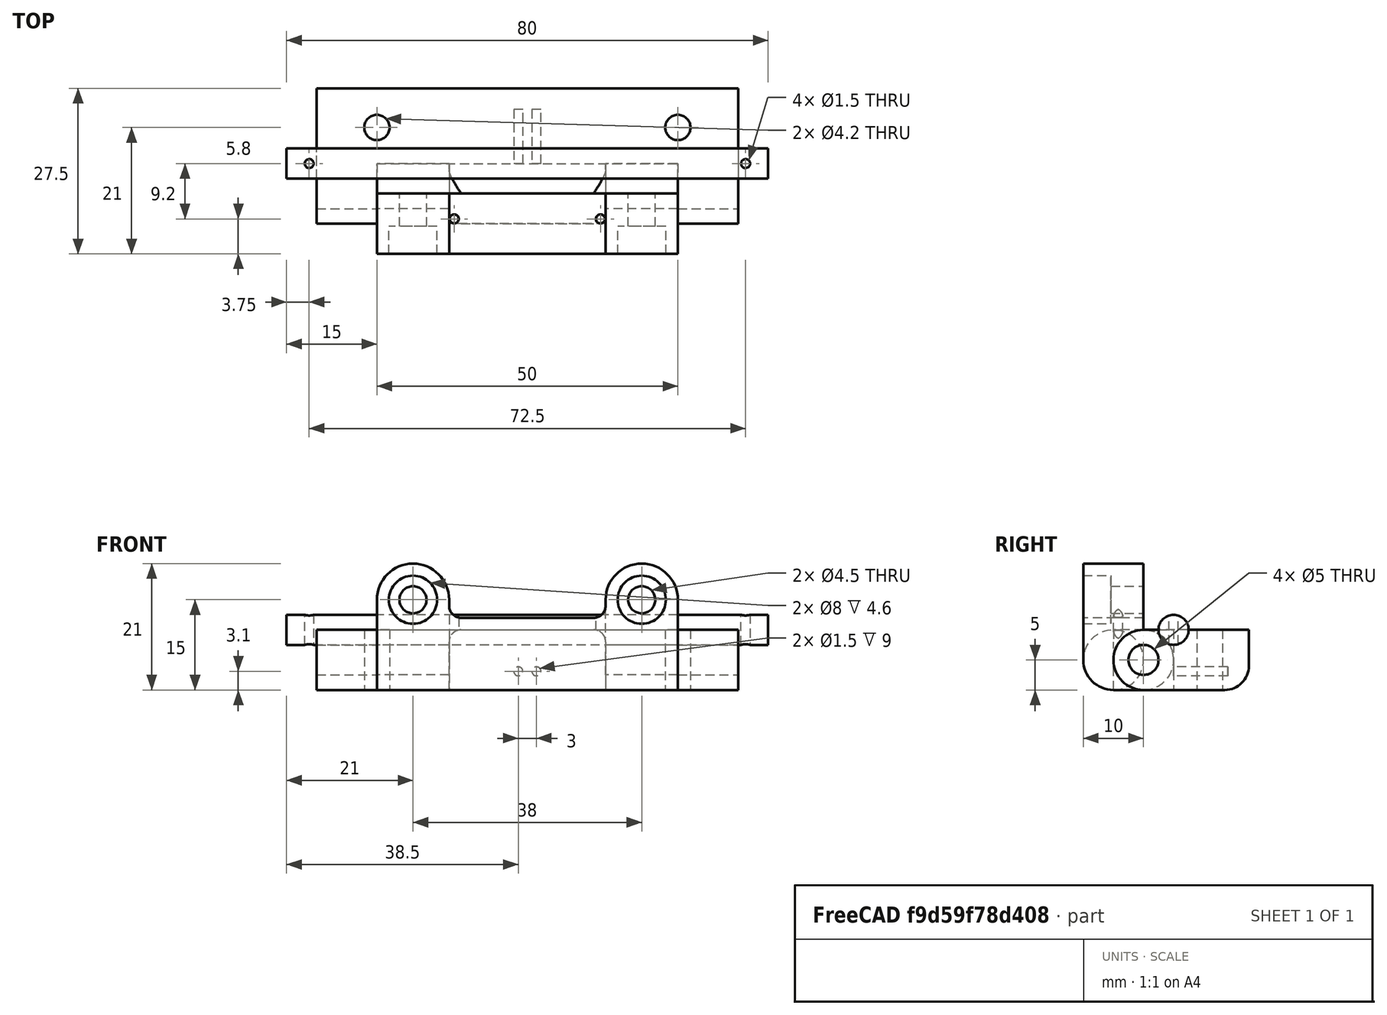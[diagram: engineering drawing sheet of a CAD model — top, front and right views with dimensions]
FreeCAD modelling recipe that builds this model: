
FCSTD DOCUMENT  (FreeCAD 0.18R14555 (Git shallow))
Label: hinge
License: All rights reserved
LicenseURL: http://en.wikipedia.org/wiki/All_rights_reserved
objects: TechDraw::DrawViewDimension×17, Sketcher::SketchObject×11, PartDesign::Pocket×6, TechDraw::DrawProjGroupItem×6, PartDesign::Pad×3, TechDraw::DrawProjGroup×3, PartDesign::Body×3, PartDesign::Hole×2, TechDraw::DrawSVGTemplate×2, TechDraw::DrawViewAnnotation×2, TechDraw::DrawViewSymbol×2, TechDraw::DrawViewPart×2, TechDraw::DrawPage×2, PartDesign::Plane×1, PartDesign::Fillet×1, TechDraw::DrawViewSection×1
note: 38 computed .brp shape members not serialized (recipe doc carries the construction recipe); baked Part::Feature solids carry a one-line shape summary decoded from their .brp

FEATURE [Sketcher::SketchObject] Sketch001
  MapMode = 5
  Support = -> [XY_Plane001]
  sketch-geometry (8):
    g0: LineSegment StartX=-35 StartY=-10 StartZ=0 EndX=-35 EndY=12.5 EndZ=0
    g1: LineSegment StartX=-35 StartY=12.5 StartZ=0 EndX=35 EndY=12.5 EndZ=0
    g2: LineSegment StartX=35 StartY=12.5 StartZ=0 EndX=35 EndY=-10 EndZ=0
    g3: LineSegment StartX=35 StartY=-10 StartZ=0 EndX=25 EndY=-10 EndZ=0
    g4: LineSegment StartX=25 StartY=-10 StartZ=0 EndX=25 EndY=0 EndZ=0
    g5: LineSegment StartX=-35 StartY=-10 StartZ=0 EndX=-25 EndY=-10 EndZ=0
    g6: LineSegment StartX=-25 StartY=-10 StartZ=0 EndX=-25 EndY=0 EndZ=0
    g7: LineSegment StartX=-25 StartY=0 StartZ=0 EndX=25 EndY=0 EndZ=0
  constraints (22):
    c: Vertical(g0)
    c: Coincident(g0,g1)
    c: Coincident(g1,g2)
    c: Vertical(g2)
    c: Coincident(g2,g3)
    c: Horizontal(g3)
    c: Coincident(g3,g4)
    c: PointOnObject(g4,g-1)
    c: Coincident(g0,g5)
    c: Horizontal(g5)
    c: Coincident(g5,g6)
    c: PointOnObject(g6,g-1)
    c: Vertical(g6)
    c: Vertical(g4)
    c: Symmetric(g1,g0,g-2)
    c: Symmetric(g3,g5,g-2)
    c: Coincident(g7,g4)
    c: DistanceX(g5,g5) = 10
    c: DistanceY(g6,g6) = 10
    c: Coincident(g7,g6)
    c: DistanceX(g5,g3) = 50
    c: DistanceY(g-1,g1) = 12.5
FEATURE [PartDesign::Pad] Pad001
  Length = 10
  Length2 = 100
  Profile = -> Sketch001
  Reversed = true
  Type = 0
FEATURE [Sketcher::SketchObject] Sketch002
  MapMode = 5
  Placement = pos=(0,0,0) rot=(0.57735,0.57735,0.57735;2.0944rad)
  Support = -> [YZ_Plane001]
  sketch-geometry (10):
    g0: Circle CenterX=-5 CenterY=-5 CenterZ=0 NormalX=0 NormalY=0 NormalZ=1 AngleXU=0 Radius=2.5
    g1: ArcOfCircle CenterX=-5 CenterY=-5 CenterZ=0 NormalX=0 NormalY=0 NormalZ=1 AngleXU=0 Radius=5 StartAngle=1.5708 EndAngle=3.14159
    g2: LineSegment [constr] StartX=-10 StartY=-5 StartZ=0 EndX=-10 EndY=0 EndZ=0
    g3: LineSegment StartX=-10 StartY=0 StartZ=0 EndX=-5 EndY=0 EndZ=0
    g4: LineSegment StartX=-10 StartY=-10 StartZ=0 EndX=-5 EndY=-10 EndZ=0
    g5: ArcOfCircle CenterX=-5 CenterY=-5 CenterZ=0 NormalX=0 NormalY=0 NormalZ=1 AngleXU=0 Radius=5 StartAngle=3.14159 EndAngle=4.71239
    g6: LineSegment [constr] StartX=-10 StartY=-5 StartZ=0 EndX=-10 EndY=-10 EndZ=0
    g7: LineSegment StartX=-10 StartY=0 StartZ=0 EndX=-13 EndY=0 EndZ=0
    g8: LineSegment StartX=-13 StartY=0 StartZ=0 EndX=-13 EndY=-10 EndZ=0
    g9: LineSegment StartX=-13 StartY=-10 StartZ=0 EndX=-10 EndY=-10 EndZ=0
  constraints (27):
    c: Diameter(g0) = 5
    c: Coincident(g1,g0)
    c: Vertical(g2)
    c: Coincident(g3,g2)
    c: Tangent(g3,g1) = 1.5708
    c: Coincident(g1,g3)
    c: Horizontal(g3)
    c: DistanceX(g0,g-1) = 5
    c: PointOnObject(g2,g-1)
    c: DistanceY(g0,g-1) = 5
    c: Horizontal(g4)
    c: Tangent(g1,g5) = -1.5708
    c: Tangent(g1,g2) = 1.5708
    c: Coincident(g6,g1)
    c: Vertical(g6)
    c: Coincident(g4,g6)
    c: Equal(g6,g2)
    c: Coincident(g3,g7)
    c: Coincident(g7,g8)
    c: Vertical(g8)
    c: Coincident(g8,g9)
    c: Coincident(g9,g4)
    c: Horizontal(g9)
    c: Horizontal(g7)
    c: DistanceX(g1,g0) = 5
    c: DistanceX(g9,g9) = 3
    c: Tangent(g5,g4) = -1.5708
FEATURE [PartDesign::Pocket] Pocket
  BaseFeature = -> Pad001
  Length = 5
  Length2 = 100
  Midplane = true
  Profile = -> Sketch002
  Type = 1
FEATURE [Sketcher::SketchObject] Sketch007
  MapMode = 5
  Support = -> [XY_Plane001]
  sketch-geometry (5):
    g0: Circle [constr] CenterX=0 CenterY=6 CenterZ=0 NormalX=0 NormalY=0 NormalZ=1 AngleXU=0 Radius=2.1
    g1: Circle CenterX=25 CenterY=6 CenterZ=0 NormalX=0 NormalY=0 NormalZ=1 AngleXU=0 Radius=2.1
    g2: Circle CenterX=-25 CenterY=6 CenterZ=0 NormalX=0 NormalY=0 NormalZ=1 AngleXU=0 Radius=2.1
    g3: LineSegment [constr] StartX=0 StartY=6 StartZ=0 EndX=25 EndY=6 EndZ=0
    g4: LineSegment [constr] StartX=0 StartY=6 StartZ=0 EndX=-25 EndY=6 EndZ=0
  constraints (13):
    c: PointOnObject(g0,g-2)
    c: Coincident(g3,g0)
    c: Coincident(g3,g1)
    c: Coincident(g4,g0)
    c: Coincident(g4,g2)
    c: Horizontal(g3)
    c: Horizontal(g4)
    c: Equal(g4,g3)
    c: DistanceX(g2,g1) = 50
    c: Diameter(g0) = 4.2
    c: Equal(g0,g1)
    c: Equal(g0,g2)
    c: DistanceY(g-1,g0) = 6
FEATURE [PartDesign::Hole] Hole
  BaseFeature = -> Pocket
  Depth = 25
  DepthType = 1
  Diameter = 4.2
  DrillPoint = 1
  DrillPointAngle = 118
  HoleCutCountersinkAngle = 90
  HoleCutDepth = 0
  HoleCutDiameter = 0
  HoleCutType = 0
  ModelActualThread = false
  Profile = -> Sketch007
  Tapered = false
  TaperedAngle = 90
  ThreadAngle = 0
  ThreadClass = 0
  ThreadCutOffInner = 0
  ThreadCutOffOuter = 0
  ThreadDirection = 0
  ThreadFit = 0
  ThreadPitch = 0
  ThreadSize = 0
  ThreadType = 0
  Threaded = false
FEATURE [Sketcher::SketchObject] Sketch
  MapMode = 5
  Placement = pos=(0,0,0) rot=(0.57735,0.57735,0.57735;2.0944rad)
  Support = -> [YZ_Plane]
  sketch-geometry (7):
    g0: Circle CenterX=-5 CenterY=-5 CenterZ=0 NormalX=0 NormalY=0 NormalZ=1 AngleXU=0 Radius=2.5
    g1: ArcOfCircle CenterX=-5 CenterY=-5 CenterZ=0 NormalX=0 NormalY=0 NormalZ=1 AngleXU=0 Radius=5 StartAngle=4.71239 EndAngle=7.85398
    g2: LineSegment StartX=-4.99997 StartY=12 StartZ=0 EndX=-15 EndY=12 EndZ=0
    g3: LineSegment StartX=-15 StartY=12 StartZ=0 EndX=-15 EndY=-5 EndZ=0
    g4: LineSegment StartX=-9.99997 StartY=-10 StartZ=0 EndX=-5 EndY=-10 EndZ=0
    g5: LineSegment StartX=-4.99997 StartY=-8.94778e-11 StartZ=0 EndX=-4.99997 EndY=12 EndZ=0
    g6: ArcOfCircle CenterX=-9.99997 CenterY=-5 CenterZ=0 NormalX=0 NormalY=0 NormalZ=1 AngleXU=0 Radius=5 StartAngle=3.14159 EndAngle=4.71239
  constraints (20):
    c: DistanceX(g0,g-1) = 5
    c: DistanceY(g0,g-1) = 5
    c: Diameter(g0) = 5
    c: Coincident(g1,g0)
    c: PointOnObject(g1,g-1)
    c: Radius(g1) = 5
    c: Horizontal(g2)
    c: Coincident(g2,g3)
    c: Vertical(g3)
    c: Coincident(g4,g1)
    c: Horizontal(g4)
    c: DistanceY(g1,g2) = 12
    c: DistanceY(g1,g0) = 5
    c: DistanceX(g2,g2) = 10
    c: Coincident(g5,g2)
    c: Vertical(g5)
    c: Tangent(g4,g6) = -1.5708
    c: Tangent(g3,g6) = -1.5708
    c: Radius(g6) = 5
    c: Coincident(g5,g1)
FEATURE [PartDesign::Pad] Pad
  Length = 50
  Length2 = 100
  Midplane = true
  Placement = pos=(0,0,0) rot=(0.57735,0.57735,0.57735;2.0944rad)
  Profile = -> Sketch
  Type = 0
FEATURE [Sketcher::SketchObject] Sketch010
  MapMode = 5
  Placement = pos=(0,0,0) rot=(1,0,0;1.5708rad)
  Support = -> [XZ_Plane]
  sketch-geometry (14):
    g0: LineSegment StartX=13 StartY=5 StartZ=0 EndX=13 EndY=4 EndZ=0
    g1: LineSegment StartX=-13 StartY=4 StartZ=0 EndX=-13 EndY=5 EndZ=0
    g2: ArcOfCircle CenterX=-19 CenterY=5 CenterZ=0 NormalX=0 NormalY=0 NormalZ=1 AngleXU=0 Radius=6 StartAngle=1e-16 EndAngle=3.14159
    g3: ArcOfCircle CenterX=19 CenterY=5 CenterZ=0 NormalX=0 NormalY=0 NormalZ=1 AngleXU=0 Radius=6 StartAngle=0 EndAngle=3.14159
    g4: LineSegment [constr] StartX=25 StartY=5 StartZ=0 EndX=-25 EndY=5 EndZ=0
    g5: LineSegment StartX=25 StartY=5 StartZ=0 EndX=25 EndY=11 EndZ=0
    g6: LineSegment [constr] StartX=25 StartY=11 StartZ=0 EndX=-25 EndY=11 EndZ=0
    g7: LineSegment StartX=-25 StartY=11 StartZ=0 EndX=-25 EndY=5 EndZ=0
    g8: LineSegment StartX=-25 StartY=11 StartZ=0 EndX=-25 EndY=12 EndZ=0
    g9: LineSegment StartX=-25 StartY=12 StartZ=0 EndX=25 EndY=12 EndZ=0
    g10: LineSegment StartX=25 StartY=12 StartZ=0 EndX=25 EndY=11 EndZ=0
    g11: LineSegment StartX=-11 StartY=2 StartZ=0 EndX=11 EndY=2 EndZ=0
    g12: ArcOfCircle CenterX=-11 CenterY=4 CenterZ=0 NormalX=0 NormalY=0 NormalZ=1 AngleXU=0 Radius=2 StartAngle=3.14159 EndAngle=4.71239
    g13: ArcOfCircle CenterX=11 CenterY=4 CenterZ=0 NormalX=0 NormalY=0 NormalZ=1 AngleXU=0 Radius=2 StartAngle=4.71239 EndAngle=6.28319
  constraints (39):
    c: Vertical(g0)
    c: Vertical(g1)
    c: Symmetric(g0,g1,g-2)
    c: DistanceX(g1,g0) = 26
    c: Coincident(g2,g1)
    c: Coincident(g3,g0)
    c: Coincident(g4,g3)
    c: Coincident(g4,g2)
    c: Horizontal(g4)
    c: PointOnObject(g2,g4)
    c: PointOnObject(g1,g4)
    c: PointOnObject(g3,g4)
    c: Equal(g3,g2)
    c: DistanceX(g4,g4) = 50
    c: Coincident(g3,g5)
    c: Coincident(g5,g6)
    c: Horizontal(g6)
    c: Coincident(g6,g7)
    c: Coincident(g7,g2)
    c: Vertical(g7)
    c: DistanceY(g-1,g6) = 11
    c: Coincident(g7,g8)
    c: Vertical(g8)
    c: Coincident(g8,g9)
    c: Horizontal(g9)
    c: Coincident(g9,g10)
    c: Coincident(g10,g5)
    c: Vertical(g10)
    c: Vertical(g5)
    c: DistanceY(g8,g8) = 1
    c: Tangent(g2,g6)
    c: Horizontal(g11)
    c: Tangent(g1,g12) = 1.5708
    c: Tangent(g11,g12) = -1.5708
    c: Radius(g12) = 2
    c: DistanceY(g-1,g11) = 2
    c: Tangent(g0,g13) = 1.5708
    c: Tangent(g11,g13) = -1.5708
    c: Equal(g13,g12)
FEATURE [PartDesign::Plane] DatumPlane001
  AttachmentOffset = pos=(0,0,15) rot=(0,0,1;0rad)
  Length = 56.4768
  MapMode = 5
  Placement = pos=(0,-15,-3.3e-15) rot=(1,0,0;1.5708rad)
  ResizeMode = 0
  Support = -> [XZ_Plane]
  Width = 27.4512
FEATURE [Sketcher::SketchObject] Sketch011
  MapMode = 5
  Placement = pos=(0,-15,-3.3e-15) rot=(1,0,0;1.5708rad)
  Support = -> [DatumPlane001]
  sketch-geometry (2):
    g0: Circle CenterX=-19 CenterY=5 CenterZ=0 NormalX=0 NormalY=0 NormalZ=1 AngleXU=0 Radius=2
    g1: Circle CenterX=19 CenterY=5 CenterZ=0 NormalX=0 NormalY=0 NormalZ=1 AngleXU=0 Radius=2.31769
  constraints (4):
    c: Symmetric(g1,g0,g-2)
    c: DistanceX(g0,g1) = 38
    c: Diameter(g0) = 4
    c: DistanceY(g-1,g0) = 5
FEATURE [Sketcher::SketchObject] Sketch009
  MapMode = 5
  Placement = pos=(0,0,0) rot=(1,0,0;1.5708rad)
  Support = -> [XZ_Plane]
  sketch-geometry (6):
    g0: LineSegment StartX=-11.0007 StartY=0 StartZ=0 EndX=10.9993 EndY=0 EndZ=0
    g1: LineSegment StartX=12.9993 StartY=-2 StartZ=0 EndX=12.9993 EndY=-18.3189 EndZ=0
    g2: LineSegment StartX=12.9993 StartY=-18.3189 StartZ=0 EndX=-13.0007 EndY=-18.3189 EndZ=0
    g3: LineSegment StartX=-13.0007 StartY=-18.3189 StartZ=0 EndX=-13.0007 EndY=-2 EndZ=0
    g4: ArcOfCircle CenterX=10.9993 CenterY=-2 CenterZ=0 NormalX=0 NormalY=0 NormalZ=1 AngleXU=0 Radius=2 StartAngle=0 EndAngle=1.5708
    g5: ArcOfCircle CenterX=-11.0007 CenterY=-2 CenterZ=0 NormalX=0 NormalY=0 NormalZ=1 AngleXU=0 Radius=2 StartAngle=1.5708 EndAngle=3.14159
  constraints (14):
    c: Coincident(g1,g2)
    c: Coincident(g2,g3)
    c: Horizontal(g2)
    c: Vertical(g1)
    c: Vertical(g3)
    c: Tangent(g1,g4) = 1.5708
    c: Tangent(g0,g4) = 1.5708
    c: Tangent(g0,g5) = 1.5708
    c: Tangent(g3,g5) = 1.5708
    c: DistanceX(g3,g1) = 26
    c: Radius(g4) = 2
    c: Equal(g4,g5)
    c: Horizontal(g0)
    c: PointOnObject(g0,g-1)
FEATURE [PartDesign::Pocket] Pocket002
  BaseFeature = -> Pad
  Length = 10
  Length2 = 100
  Placement = pos=(0,0,0) rot=(0.57735,0.57735,0.57735;2.0944rad)
  Profile = -> Sketch009
  Reversed = true
  Type = 0
FEATURE [PartDesign::Pocket] Pocket003
  BaseFeature = -> Pocket002
  Length = 5
  Length2 = 100
  Placement = pos=(0,0,0) rot=(0.57735,0.57735,0.57735;2.0944rad)
  Profile = -> Sketch010
  Reversed = true
  Type = 1
FEATURE [TechDraw::DrawSVGTemplate] Template
  EditableTexts = Designed_by_Name=Papamatthaiou M.; FC-Date=17/01/2020; FC-SC=1:1; FC-SHEET=1/1; FC-Title=PocketQube Static Hinge; MATERIAL=NOTE-4; REV=B; ROUGHNESS=-; Subtitle=StatikHinge; TOLERANCES=DIN ISO 2768-mk; Weight=~26.56g
  Height = 210
  Orientation = 1
  Width = 297
FEATURE [TechDraw::DrawProjGroup] ProjGroup
  AutoDistribute = true
  LockPosition = false
  ProjectionType = 1
  Rotation = 0
  ScaleType = 2
  X = 168.228
  Y = 97.2357
  spacingX = 15
  spacingY = 15
FEATURE [TechDraw::DrawViewAnnotation] Annotation
  Font = DejaVu Sans
  LineSpace = 80
  LockPosition = false
  MaxWidth = -1
  Rotation = 0
  ScaleType = 0
  Text = Notes: | 1. Drill hole \u23004.2 THRU | 2. Mating hole (H7) for part P/N:  | MISUMI  SCLGN5-70 Shaft Dia. D: 5.00,  | Tolerance: g6 (sliding fit) | 3. This part is mating with parts DoorHinge | and with y-plate | 4. Material: Al 7075 | 5. Drill hole \u23001.5 THRU. Mating holes  | for torsional springs
  TextSize = 6
  TextStyle = 0
  X = 77.2478
  Y = 49.013
FEATURE [PartDesign::Hole] Hole001
  BaseFeature = -> Pocket003
  Depth = 25
  DepthType = 1
  Diameter = 4.5
  DrillPoint = 1
  DrillPointAngle = 118
  HoleCutCountersinkAngle = 90
  HoleCutDepth = 4.6
  HoleCutDiameter = 8
  HoleCutType = 1
  ModelActualThread = false
  Placement = pos=(0,0,0) rot=(0.57735,0.57735,0.57735;2.0944rad)
  Profile = -> Sketch011
  Tapered = false
  TaperedAngle = 90
  ThreadAngle = 0
  ThreadClass = 0
  ThreadCutOffInner = 0
  ThreadCutOffOuter = 0
  ThreadDirection = 0
  ThreadFit = 0
  ThreadPitch = 0
  ThreadSize = 0
  ThreadType = 0
  Threaded = false
FEATURE [TechDraw::DrawSVGTemplate] Template001
  EditableTexts = Designed_by_Name=Papamatthaiou M.; FC-Date=17/01/2020; FC-SC=1:1; FC-SHEET=1/1; FC-Title=PocketQube Door Hinge; MATERIAL=NOTE-5; REV=B; ROUGHNESS=-; Subtitle=DoorHinge; TOLERANCES=DIN ISO 2768-mk; Weight=~17.21g
  Height = 210
  Orientation = 1
  Width = 297
FEATURE [TechDraw::DrawViewSymbol] Symbol
  LockPosition = false
  Rotation = 0
  ScaleType = 2
  Symbol = <blob: 3150 chars omitted>
  X = 16.0884
  Y = 131.565
FEATURE [TechDraw::DrawViewSymbol] Symbol001
  LockPosition = false
  Rotation = 0
  ScaleType = 2
  Symbol = <blob: 3150 chars omitted>
  X = 22.4016
  Y = 147.366
FEATURE [TechDraw::DrawViewAnnotation] Annotation001
  Font = DejaVu Sans
  LineSpace = 80
  LockPosition = false
  MaxWidth = -1
  Rotation = 0
  ScaleType = 0
  Text = Notes: | 1. Drill hole \u23004.5 THRU | 2. Mating hole (H7) for part P/N:  | MISUMI  SCLGN5-70 Shaft Dia. D: 5.00,  | Tolerance: g6 (sliding fit) | 3. This part is mating with parts DoorHinge | and with door | 4. CBORE \u23008.00 DEEP 4.6 (M4 DIN912) | 5. Material: Al 7075 | 6. Drill Holes \u23001.5 THRU. Mating | holes for torsional springs
  TextSize = 6
  TextStyle = 0
  X = 77.0938
  Y = 51.4062
FEATURE [Sketcher::SketchObject] Sketch012
  MapMode = 5
  Placement = pos=(0,0,0) rot=(1,0,0;1.5708rad)
  Support = -> [XZ_Plane001]
  sketch-geometry (3):
    g0: Circle CenterX=-1.5 CenterY=-6.9 CenterZ=0 NormalX=0 NormalY=0 NormalZ=1 AngleXU=0 Radius=0.75
    g1: Circle CenterX=1.5 CenterY=-6.9 CenterZ=0 NormalX=0 NormalY=0 NormalZ=1 AngleXU=0 Radius=0.75
    g2: GeomPoint X=0 Y=-10 Z=0
  constraints (7):
    c: Diameter(g1) = 1.5
    c: Equal(g1,g0)
    c: Symmetric(g1,g0,g-2)
    c: DistanceX(g0,g1) = 3
    c: PointOnObject(g2,g-2)
    c: DistanceY(g2,g-1) = 10
    c: DistanceY(g2,g1) = 3.1
FEATURE [PartDesign::Pocket] Pocket004
  BaseFeature = -> Hole
  Length = 9
  Length2 = 100
  Profile = -> Sketch012
  Type = 0
FEATURE [PartDesign::Fillet] Fillet
  Base = -> Pocket004 [Edge19]
  BaseFeature = -> Pocket004
  Radius = 4
FEATURE [PartDesign::Body] Body001  label="StatikHinge"
  Group = -> [Sketch001,Pad001,Sketch002,Pocket,Sketch007,Hole,Sketch012,Pocket004,Fillet]
  Origin = -> Origin001
  Tip = -> Fillet
FEATURE [TechDraw::DrawViewPart] View
  CoarseView = false
  Direction = (0.831,-0.177,0.527)
  Focus = 100
  HardHidden = false
  IsoCount = 0
  IsoHidden = false
  IsoVisible = false
  LockPosition = false
  Perspective = false
  Rotation = 0
  ScaleType = 0
  SeamHidden = false
  SeamVisible = false
  SmoothHidden = false
  SmoothVisible = false
  Source = -> [Body001]
  X = 260.762
  Y = 173.153
FEATURE [Sketcher::SketchObject] Sketch013
  MapMode = 5
  Support = -> [XY_Plane]
  sketch-geometry (2):
    g0: Circle CenterX=-12.15 CenterY=-9.2 CenterZ=0 NormalX=0 NormalY=0 NormalZ=1 AngleXU=0 Radius=0.75
    g1: Circle CenterX=12.15 CenterY=-9.2 CenterZ=0 NormalX=0 NormalY=0 NormalZ=1 AngleXU=0 Radius=0.75
  constraints (5):
    c: Diameter(g1) = 1.5
    c: Equal(g1,g0)
    c: Symmetric(g0,g1,g-2)
    c: DistanceX(g0,g1) = 24.3
    c: DistanceY(g1,g-1) = 9.2
FEATURE [PartDesign::Pocket] Pocket005
  BaseFeature = -> Hole001
  Length = 5
  Length2 = 100
  Midplane = true
  Placement = pos=(0,0,0) rot=(0.57735,0.57735,0.57735;2.0944rad)
  Profile = -> Sketch013
  Type = 1
FEATURE [PartDesign::Body] Body  label="DoorHinge"
  Group = -> [Sketch,Pad,Sketch009,Pocket002,Sketch010,Pocket003,DatumPlane001,Sketch011,Hole001,Sketch013,Pocket005]
  Origin = -> Origin
  Tip = -> Pocket005
FEATURE [TechDraw::DrawProjGroupItem] ProjItem002  label="Front001"
  CoarseView = false
  Direction = (0,1,0)
  Focus = 100
  HardHidden = false
  IsoCount = 0
  IsoHidden = false
  IsoVisible = false
  LockPosition = true
  Perspective = false
  Rotation = 0
  RotationVector = (-1,0,0)
  ScaleType = 2
  SeamHidden = false
  SeamVisible = false
  SmoothHidden = false
  SmoothVisible = false
  Source = -> [Body]
  Type = 0
  X = 0
  Y = 0
FEATURE [TechDraw::DrawProjGroupItem] ProjItem003  label="Left001"
  CoarseView = false
  Direction = (1,1e-16,0)
  Focus = 100
  HardHidden = false
  IsoCount = 0
  IsoHidden = false
  IsoVisible = false
  LockPosition = false
  Perspective = false
  Rotation = 0
  RotationVector = (-1e-16,1,0)
  ScaleType = 2
  SeamHidden = false
  SeamVisible = false
  SmoothHidden = false
  SmoothVisible = false
  Source = -> [Body]
  Type = 1
  X = 65
  Y = 0
FEATURE [TechDraw::DrawViewDimension] Dimension007
  Arbitrary = false
  FormatSpec = (Note-1) ⌀%.2f
  LockPosition = false
  MeasureType = 1
  OverTolerance = 0
  References2D = -> [ProjItem002]
  Rotation = 0
  ScaleType = 0
  Type = 5
  UnderTolerance = 0
  X = 5.54075
  Y = 26.0395
FEATURE [TechDraw::DrawViewDimension] Dimension008
  Arbitrary = false
  FormatSpec = (Note-2) ⌀%.2fH7
  LockPosition = false
  MeasureType = 1
  OverTolerance = 0
  References2D = -> [ProjItem003]
  Rotation = 0
  ScaleType = 0
  Type = 5
  UnderTolerance = 0
  X = 38.605
  Y = 5.77784
FEATURE [TechDraw::DrawViewPart] View002
  CoarseView = false
  Direction = (-0.669,0.732,-0.128)
  Focus = 100
  HardHidden = false
  IsoCount = 0
  IsoHidden = false
  IsoVisible = false
  LockPosition = false
  Perspective = false
  Rotation = 0
  ScaleType = 0
  SeamHidden = false
  SeamVisible = false
  SmoothHidden = false
  SmoothVisible = false
  Source = -> [Body]
  X = 259.541
  Y = 183.599
FEATURE [TechDraw::DrawViewSection] DrawViewSection  label="Section B - B"
  BaseView = -> ProjItem002
  CoarseView = false
  Direction = (1,0,0)
  FileHatchPattern = <path>
  Focus = 100
  FuseBeforeCut = true
  HardHidden = false
  HatchScale = 1
  IsoCount = 0
  IsoHidden = false
  IsoVisible = false
  LockPosition = false
  NameGeomPattern = Diamond
  Perspective = false
  Rotation = 0
  ScaleType = 0
  SeamHidden = false
  SeamVisible = false
  SectionDirection = 0
  SectionNormal = (1,0,0)
  SectionOrigin = (-19,-7.5,0.5)
  SectionSymbol = B
  SmoothHidden = false
  SmoothVisible = false
  Source = -> [Body]
  X = 240.508
  Y = 105.408
FEATURE [TechDraw::DrawViewDimension] Dimension010
  Arbitrary = false
  FormatSpec = (Note-4) %.2f
  LockPosition = false
  MeasureType = 1
  OverTolerance = 0
  References2D = -> [DrawViewSection]
  Rotation = 0
  ScaleType = 0
  Type = 2
  UnderTolerance = 0
  X = -32.2034
  Y = -16.2929
FEATURE [TechDraw::DrawProjGroupItem] ProjItem004  label="Front002"
  CoarseView = false
  Direction = (0,0,1)
  Focus = 100
  HardHidden = false
  IsoCount = 0
  IsoHidden = false
  IsoVisible = false
  LockPosition = true
  Perspective = false
  Rotation = 0
  RotationVector = (1,0,0)
  ScaleType = 2
  SeamHidden = false
  SeamVisible = false
  SmoothHidden = false
  SmoothVisible = false
  Source = -> [Fillet]
  Type = 0
  X = 0
  Y = 0
FEATURE [TechDraw::DrawProjGroupItem] ProjItem005  label="Left002"
  CoarseView = false
  Direction = (-1,0,1e-16)
  Focus = 100
  HardHidden = false
  IsoCount = 0
  IsoHidden = false
  IsoVisible = false
  LockPosition = false
  Perspective = false
  Rotation = 0
  RotationVector = (1e-16,0,1)
  ScaleType = 2
  SeamHidden = false
  SeamVisible = false
  SmoothHidden = false
  SmoothVisible = false
  Source = -> [Fillet]
  Type = 1
  X = 85
  Y = 0
FEATURE [TechDraw::DrawViewDimension] Dimension012
  Arbitrary = false
  FormatSpec = (Note-3) %.2f
  LockPosition = false
  MeasureType = 1
  OverTolerance = 0.1
  References2D = -> [ProjItem004]
  Rotation = 0
  ScaleType = 0
  Type = 1
  UnderTolerance = 0
  X = -1.46419
  Y = -24.1349
FEATURE [TechDraw::DrawViewDimension] Dimension013
  Arbitrary = false
  FormatSpec = %.2f
  LockPosition = false
  MeasureType = 1
  OverTolerance = 0
  References2D = -> [ProjItem004]
  Rotation = 0
  ScaleType = 0
  Type = 1
  UnderTolerance = -0.2
  X = -2.04987
  Y = -35.5556
FEATURE [TechDraw::DrawProjGroupItem] ProjItem006  label="Bottom"
  CoarseView = false
  Direction = (0,-1,0)
  Focus = 100
  HardHidden = false
  IsoCount = 0
  IsoHidden = false
  IsoVisible = false
  LockPosition = false
  Perspective = false
  Rotation = 0
  RotationVector = (1,0,0)
  ScaleType = 2
  SeamHidden = false
  SeamVisible = false
  SmoothHidden = false
  SmoothVisible = false
  Source = -> [Fillet]
  Type = 5
  X = 0
  Y = 37.5
FEATURE [TechDraw::DrawProjGroup] ProjGroup002
  Anchor = -> ProjItem004
  AutoDistribute = true
  LockPosition = false
  ProjectionType = 1
  Rotation = 0
  ScaleType = 2
  Source = -> [Fillet]
  Views = -> [ProjItem004,ProjItem005,ProjItem006]
  X = 88.691
  Y = 138.45
  spacingX = 15
  spacingY = 15
FEATURE [TechDraw::DrawViewDimension] Dimension014
  Arbitrary = false
  FormatSpec = (Note-1) ⌀%.2f 
  LockPosition = false
  MeasureType = 1
  OverTolerance = 0
  References2D = -> [ProjItem004]
  Rotation = 0
  ScaleType = 0
  Type = 5
  UnderTolerance = 0
  X = 0.44554
  Y = 19.6037
FEATURE [TechDraw::DrawViewDimension] Dimension015
  Arbitrary = false
  FormatSpec = (Note-2) ⌀%.2fH7
  LockPosition = false
  MeasureType = 1
  OverTolerance = 0
  References2D = -> [ProjItem005]
  Rotation = 0
  ScaleType = 0
  Type = 5
  UnderTolerance = 0
  X = 32.9699
  Y = 6.01477
FEATURE [TechDraw::DrawViewDimension] Dimension016
  Arbitrary = false
  FormatSpec = %.2f
  LockPosition = false
  MeasureType = 1
  OverTolerance = 0.1
  References2D = -> [ProjItem005]
  Rotation = 0
  ScaleType = 0
  Type = 2
  UnderTolerance = -0.1
  X = -21.2176
  Y = 29.9006
FEATURE [TechDraw::DrawViewDimension] Dimension
  Arbitrary = false
  FormatSpec = %.2f
  LockPosition = false
  MeasureType = 1
  OverTolerance = 0.1
  References2D = -> [ProjItem006]
  Rotation = 0
  ScaleType = 0
  Type = 2
  UnderTolerance = 0
  X = -59.5871
  Y = 7.81223
FEATURE [TechDraw::DrawViewDimension] Dimension017
  Arbitrary = false
  FormatSpec = %.2f
  LockPosition = false
  MeasureType = 1
  OverTolerance = 0.1
  References2D = -> [ProjItem006]
  Rotation = 0
  ScaleType = 0
  Type = 1
  UnderTolerance = -0.1
  X = -20.6451
  Y = 17.6805
FEATURE [TechDraw::DrawViewDimension] Dimension018
  Arbitrary = false
  FormatSpec = (Note-5) ⌀%.2f
  LockPosition = false
  MeasureType = 1
  OverTolerance = 0
  References2D = -> [ProjItem006]
  Rotation = 0
  ScaleType = 0
  Type = 5
  UnderTolerance = 0
  X = 34.1246
  Y = 16.7219
FEATURE [TechDraw::DrawPage] Page
  KeepUpdated = true
  ProjectionType = 0
  Template = -> Template
  Views = -> [ProjGroup,View,Annotation,Symbol,ProjGroup002,Dimension012,Dimension013,Dimension014,Dimension015,Dimension016,Dimension,Dimension017,Dimension018]
FEATURE [TechDraw::DrawProjGroupItem] ProjItem007  label="Top"
  CoarseView = false
  Direction = (0,0,1)
  Focus = 100
  HardHidden = false
  IsoCount = 0
  IsoHidden = false
  IsoVisible = false
  LockPosition = true
  Perspective = false
  Rotation = 0
  RotationVector = (-1,0,0)
  ScaleType = 2
  SeamHidden = false
  SeamVisible = false
  SmoothHidden = false
  SmoothVisible = false
  Source = -> [Body]
  Type = 4
  X = 0
  Y = -42.1726
FEATURE [TechDraw::DrawProjGroup] ProjGroup001
  Anchor = -> ProjItem002
  AutoDistribute = true
  LockPosition = false
  ProjectionType = 1
  Rotation = 0
  ScaleType = 2
  Source = -> [Body]
  Views = -> [ProjItem002,ProjItem003,ProjItem007]
  X = 86.3263
  Y = 154.205
  spacingX = 15
  spacingY = 15
FEATURE [TechDraw::DrawViewDimension] Dimension019
  Arbitrary = false
  FormatSpec = (Note-3) %.2f
  LockPosition = false
  MeasureType = 1
  OverTolerance = 0
  References2D = -> [ProjItem002]
  Rotation = 0
  ScaleType = 0
  Type = 1
  UnderTolerance = -0.1
  X = -2.96872
  Y = -23.0803
FEATURE [TechDraw::DrawViewDimension] Dimension020
  Arbitrary = false
  FormatSpec = (Note-3) R%.2f
  LockPosition = false
  MeasureType = 1
  OverTolerance = 0
  References2D = -> [ProjItem003]
  Rotation = 0
  ScaleType = 0
  Type = 4
  UnderTolerance = -0.1
  X = 39.0019
  Y = -15.3008
FEATURE [TechDraw::DrawViewDimension] Dimension021
  Arbitrary = false
  FormatSpec = %.2f
  LockPosition = false
  MeasureType = 1
  OverTolerance = 0.1
  References2D = -> [ProjItem007]
  Rotation = 0
  ScaleType = 0
  Type = 1
  UnderTolerance = 0
  X = 3.06171
  Y = -19.944
FEATURE [TechDraw::DrawViewDimension] Dimension022
  Arbitrary = false
  FormatSpec = %.2f
  LockPosition = false
  MeasureType = 1
  OverTolerance = 0.1
  References2D = -> [ProjItem007]
  Rotation = 0
  ScaleType = 0
  Type = 2
  UnderTolerance = -0.1
  X = -52.0507
  Y = -9.25974
FEATURE [TechDraw::DrawViewDimension] Dimension023
  Arbitrary = false
  FormatSpec = (Note-6) ⌀%.2f
  LockPosition = false
  MeasureType = 1
  OverTolerance = 0
  References2D = -> [ProjItem007]
  Rotation = 0
  ScaleType = 0
  Type = 5
  UnderTolerance = 0
  X = 48.8253
  Y = 8.96625
FEATURE [TechDraw::DrawViewDimension] Dimension024
  Arbitrary = false
  FormatSpec = %.2f
  LockPosition = false
  MeasureType = 1
  OverTolerance = 0.1
  References2D = -> [DrawViewSection]
  Rotation = 0
  ScaleType = 0
  Type = 2
  UnderTolerance = -0.1
  X = 14.5552
  Y = 19.9011
FEATURE [TechDraw::DrawPage] Page001
  KeepUpdated = true
  ProjectionType = 0
  Template = -> Template001
  Views = -> [ProjGroup001,Dimension007,Dimension008,Symbol001,View002,Annotation001,DrawViewSection,Dimension010,Dimension019,Dimension020,Dimension021,Dimension022,Dimension023,Dimension024]
FEATURE [Sketcher::SketchObject] Sketch014
  MapMode = 5
  Placement = pos=(0,0,0) rot=(0.57735,0.57735,0.57735;2.0944rad)
  Support = -> [YZ_Plane002]
  sketch-geometry (1):
    g0: Circle CenterX=0 CenterY=0 CenterZ=0 NormalX=0 NormalY=0 NormalZ=1 AngleXU=0 Radius=2.5
  constraints (2):
    c: Coincident(g0,g-1)
    c: Diameter(g0) = 5
FEATURE [PartDesign::Pad] Pad002
  Length = 80
  Length2 = 100
  Midplane = true
  Placement = pos=(0,0,0) rot=(0.57735,0.57735,0.57735;2.0944rad)
  Profile = -> Sketch014
  Type = 0
FEATURE [Sketcher::SketchObject] Sketch015
  MapMode = 5
  Support = -> [XY_Plane002]
  sketch-geometry (4):
    g0: Circle CenterX=36.25 CenterY=0 CenterZ=0 NormalX=0 NormalY=0 NormalZ=1 AngleXU=0 Radius=0.75
    g1: Circle CenterX=-36.25 CenterY=0 CenterZ=0 NormalX=0 NormalY=0 NormalZ=1 AngleXU=0 Radius=0.75
    g2: GeomPoint X=-35.5 Y=0 Z=0
    g3: GeomPoint X=35.5 Y=0 Z=0
  constraints (9):
    c: PointOnObject(g0,g-1)
    c: PointOnObject(g1,g-1)
    c: PointOnObject(g2,g-1)
    c: PointOnObject(g3,g0)
    c: PointOnObject(g2,g1)
    c: Symmetric(g2,g3,g-2)
    c: DistanceX(g2,g3) = 71
    c: Diameter(g1) = 1.5
    c: Equal(g1,g0)
FEATURE [PartDesign::Pocket] Pocket006
  BaseFeature = -> Pad002
  Length = 5
  Length2 = 100
  Midplane = true
  Placement = pos=(0,0,0) rot=(0.57735,0.57735,0.57735;2.0944rad)
  Profile = -> Sketch015
  Type = 1
FEATURE [PartDesign::Body] Body002  label="Pin"
  Group = -> [Sketch014,Pad002,Sketch015,Pocket006]
  Origin = -> Origin002
  Tip = -> Pocket006
note: 1 file-system path scrubbed to <path> (originals preserved in the JSON sidecar)
